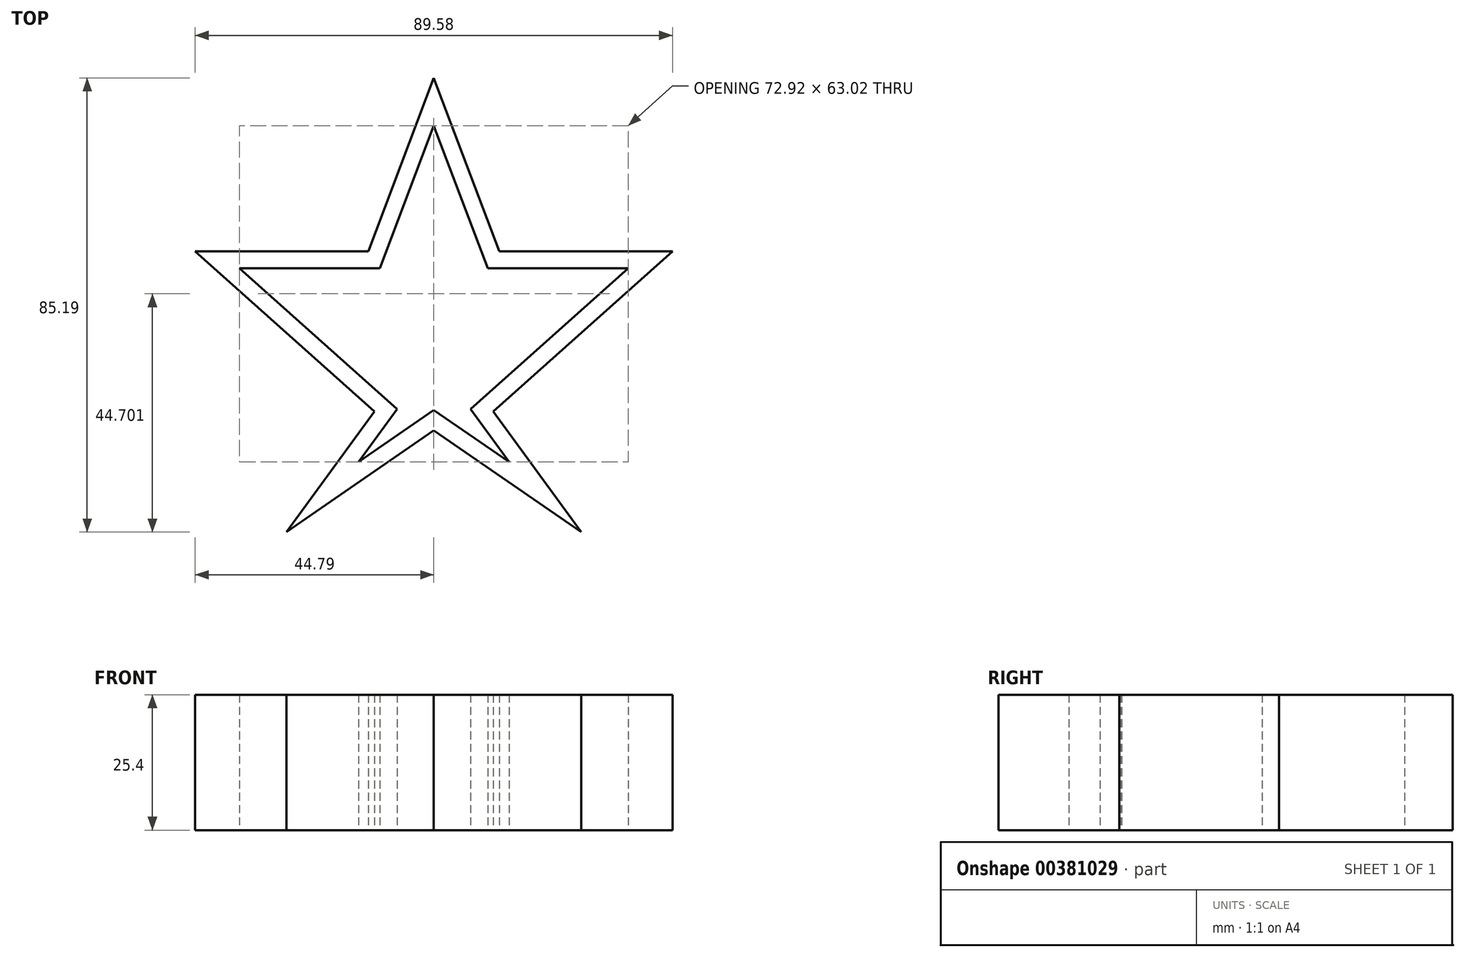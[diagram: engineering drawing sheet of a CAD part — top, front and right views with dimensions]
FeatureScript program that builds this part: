
annotation { "Feature Type Name" : "Feature", "Feature Type Description" : "" }
export const myFeature = defineFeature(function(context is Context, id is Id, definition is map)
    precondition{}
    {
        {
            var Q0;
            Q0=qCreatedBy(makeId("Top.planeOp"),FACE);
            var sketch = newSketch(context, id + "F0", { "sketchPlane" : qUnion([Q0])});
            skCircle(sketch, "E0.cCircle", {"center": v(0, 0) * mm, "radius": 38.1 * mm, "construction": true});
            skLineSegment(sketch, "E0.0", {"start": v(-44.79, 14.55) * mm, "end": v(0, 47.1) * mm, "construction": true});
            skLineSegment(sketch, "E0.1", {"start": v(0, 47.1) * mm, "end": v(44.79, 14.55) * mm, "construction": true});
            skLineSegment(sketch, "E0.2", {"start": v(44.79, 14.55) * mm, "end": v(27.68, -38.1) * mm, "construction": true});
            skLineSegment(sketch, "E0.3", {"start": v(27.68, -38.1) * mm, "end": v(-27.68, -38.1) * mm, "construction": true});
            skLineSegment(sketch, "E0.4", {"start": v(-27.68, -38.1) * mm, "end": v(-44.79, 14.55) * mm, "construction": true});
            skPoint(sketch, "E0.0.midPoint", {"position": v(-22.4, 30.82) * mm});
            skCircle(sketch, "E1", {"center": v(0, 0) * mm, "radius": 19.05 * mm, "construction": true});
            skLineSegment(sketch, "E2", {"start": v(-27.68, -38.1) * mm, "end": v(0, -19.05) * mm});
            skLineSegment(sketch, "E3", {"start": v(0, -19.05) * mm, "end": v(27.68, -38.1) * mm});
            skLineSegment(sketch, "E4", {"start": v(44.79, 14.55) * mm, "end": v(12.3, 14.55) * mm});
            skLineSegment(sketch, "E5", {"start": v(-44.79, 14.55) * mm, "end": v(-11.14, -15.45) * mm});
            skLineSegment(sketch, "E6", {"start": v(-11.14, -15.45) * mm, "end": v(-27.68, -38.1) * mm});
            skLineSegment(sketch, "E7", {"start": v(44.79, 14.55) * mm, "end": v(11.14, -15.45) * mm});
            skLineSegment(sketch, "E8", {"start": v(11.14, -15.45) * mm, "end": v(27.68, -38.1) * mm});
            skLineSegment(sketch, "E9", {"start": v(0, 47.1) * mm, "end": v(-12.3, 14.55) * mm});
            skLineSegment(sketch, "E10", {"start": v(-12.3, 14.55) * mm, "end": v(0, 47.1) * mm});
            skLineSegment(sketch, "E11", {"start": v(0, 47.1) * mm, "end": v(12.3, 14.55) * mm});
            skLineSegment(sketch, "E12.trimOffspring", {"start": v(-12.3, 14.55) * mm, "end": v(-44.79, 14.55) * mm});
            skLineSegment(sketch, "E13.0", {"start": v(-10.1, 11.38) * mm, "end": v(-36.46, 11.38) * mm});
            skLineSegment(sketch, "E13.1", {"start": v(-36.46, 11.38) * mm, "end": v(-6.88, -15) * mm});
            skLineSegment(sketch, "E13.2", {"start": v(-10.1, 11.38) * mm, "end": v(0, 38.1) * mm});
            skLineSegment(sketch, "E13.3", {"start": v(-6.88, -15) * mm, "end": v(-14.11, -24.9) * mm});
            skLineSegment(sketch, "E13.4", {"start": v(-14.11, -24.9) * mm, "end": v(0, -15.2) * mm});
            skLineSegment(sketch, "E13.5", {"start": v(0, -15.2) * mm, "end": v(14.11, -24.9) * mm});
            skLineSegment(sketch, "E13.6", {"start": v(0, 38.1) * mm, "end": v(10.1, 11.38) * mm});
            skLineSegment(sketch, "E13.7", {"start": v(36.46, 11.38) * mm, "end": v(10.1, 11.38) * mm});
            skLineSegment(sketch, "E13.8", {"start": v(36.46, 11.38) * mm, "end": v(6.88, -15) * mm});
            skLineSegment(sketch, "E13.9", {"start": v(6.88, -15) * mm, "end": v(14.11, -24.9) * mm});
            skSolve(sketch);
        }
        {
            var Q0;
            Q0 = qSketchRegion(id + "F0", true);
            extrude(context, id + "F1", {"entities" : qUnion([Q0]), "depth" : 25.4 * mm});
        }
    });
